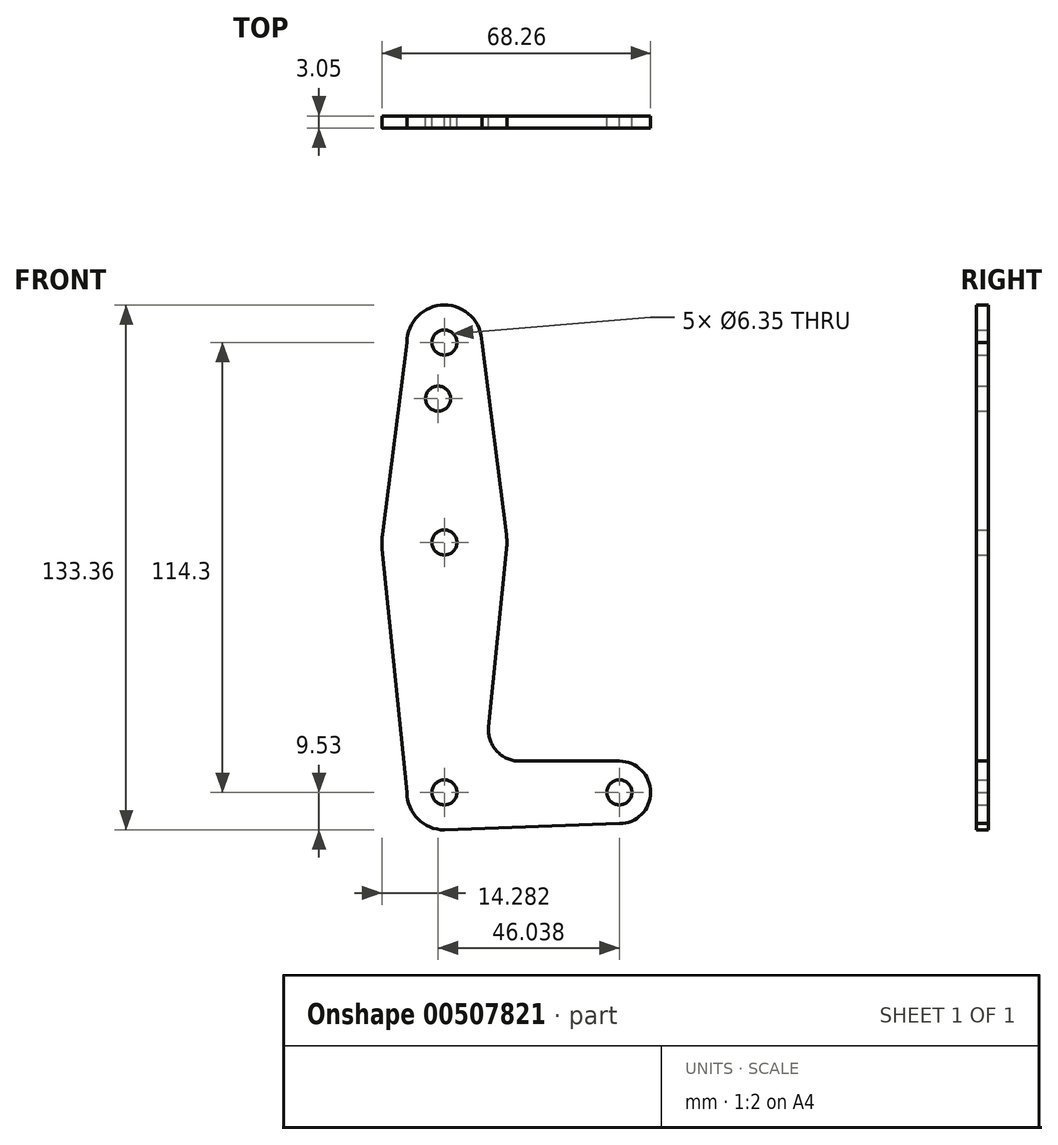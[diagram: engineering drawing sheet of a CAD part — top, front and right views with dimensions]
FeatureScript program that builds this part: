
annotation { "Feature Type Name" : "Feature", "Feature Type Description" : "" }
export const myFeature = defineFeature(function(context is Context, id is Id, definition is map)
    precondition{}
    {
        {
            var Q0;
            Q0=qCreatedBy(makeId("Front.planeOp"),FACE);
            var sketch = newSketch(context, id + "F0", { "sketchPlane" : qUnion([Q0])});
            skLineSegment(sketch, "E0", {"start": v(0, 0) * mm, "end": v(0, 114.3) * mm, "construction": true});
            skLineSegment(sketch, "E1", {"start": v(0, 0) * mm, "end": v(44.45, 0) * mm, "construction": true});
            skCircle(sketch, "E2", {"center": v(0, 0) * mm, "radius": 9.53 * mm});
            skCircle(sketch, "E3", {"center": v(0, 114.3) * mm, "radius": 9.53 * mm});
            skCircle(sketch, "E4", {"center": v(44.45, 0) * mm, "radius": 7.94 * mm});
            skCircle(sketch, "E5", {"center": v(0, 63.5) * mm, "radius": 15.88 * mm});
            skLineSegment(sketch, "E6", {"start": v(-9.53, 114.3) * mm, "end": v(-15.75, 65.5) * mm});
            skLineSegment(sketch, "E7", {"start": v(9.53, 114.3) * mm, "end": v(15.75, 65.5) * mm});
            skLineSegment(sketch, "E8", {"start": v(15.8, 61.9) * mm, "end": v(11.22, 16.69) * mm});
            skLineSegment(sketch, "E9", {"start": v(-9.53, 0) * mm, "end": v(-15.8, 61.9) * mm});
            skLineSegment(sketch, "E10", {"start": v(19.12, 7.94) * mm, "end": v(44.45, 7.94) * mm});
            skLineSegment(sketch, "E11", {"start": v(0, -9.52) * mm, "end": v(44.45, -7.94) * mm});
            skCircle(sketch, "E12", {"center": v(0, 114.3) * mm, "radius": 3.18 * mm});
            skCircle(sketch, "E13", {"center": v(0, 63.5) * mm, "radius": 3.18 * mm});
            skCircle(sketch, "E14", {"center": v(0, 0) * mm, "radius": 3.18 * mm});
            skCircle(sketch, "E15", {"center": v(44.45, 0) * mm, "radius": 3.18 * mm});
            skCircle(sketch, "E16", {"center": v(-1.59, 100.03) * mm, "radius": 3.18 * mm});
            skArc(sketch, "E17.filletArc", {"start": v(11.22, 16.69) * mm, "mid": v(13.23, 10.56) * mm, "end": v(19.12, 7.94) * mm});
            skSolve(sketch);
        }
        {
            var Q0;
            {var subQ0=sQuery(id+"F0.wireOp",EDGE,"E8");Q0=makeQuery(id+"F0.imprint","IMPRINT",FACE,{"disambiguationData":[TD([[makeQuery(id+"F0.imprint","IMPRINT",EDGE,{"derivedFrom":subQ0}),-1.0]])]});}
            var Q1;
            Q1=makeQuery(id+"F0.imprint","IMPRINT",FACE,{"disambiguationData":[TD([[makeQuery(id+"F0.imprint","IMPRINT",EDGE,{"derivedFrom":sQuery(id+"F0.wireOp",EDGE,"E14")}),-1.0]])]});
            var Q2;
            Q2=makeQuery(id+"F0.imprint","IMPRINT",FACE,{"disambiguationData":[TD([[makeQuery(id+"F0.imprint","IMPRINT",EDGE,{"derivedFrom":sQuery(id+"F0.wireOp",EDGE,"E12")}),-1.0]])]});
            var Q3;
            Q3=makeQuery(id+"F0.imprint","IMPRINT",FACE,{"disambiguationData":[TD([[makeQuery(id+"F0.imprint","IMPRINT",EDGE,{"derivedFrom":sQuery(id+"F0.wireOp",EDGE,"E15")}),-1.0]])]});
            var Q4;
            {var subQ0=sQuery(id+"F0.wireOp",EDGE,"E6");Q4=makeQuery(id+"F0.imprint","IMPRINT",FACE,{"disambiguationData":[TD([[makeQuery(id+"F0.imprint","IMPRINT",EDGE,{"derivedFrom":subQ0}),1.0]])]});}
            var Q5;
            Q5=makeQuery(id+"F0.imprint","IMPRINT",FACE,{"disambiguationData":[TD([[makeQuery(id+"F0.imprint","IMPRINT",EDGE,{"derivedFrom":sQuery(id+"F0.wireOp",EDGE,"E13")}),-1.0]])]});
            extrude(context, id + "F1", {"entities" : qUnion([Q0, Q1, Q2, Q3, Q4, Q5]), "depth" : 3.05 * mm});
        }
    });
